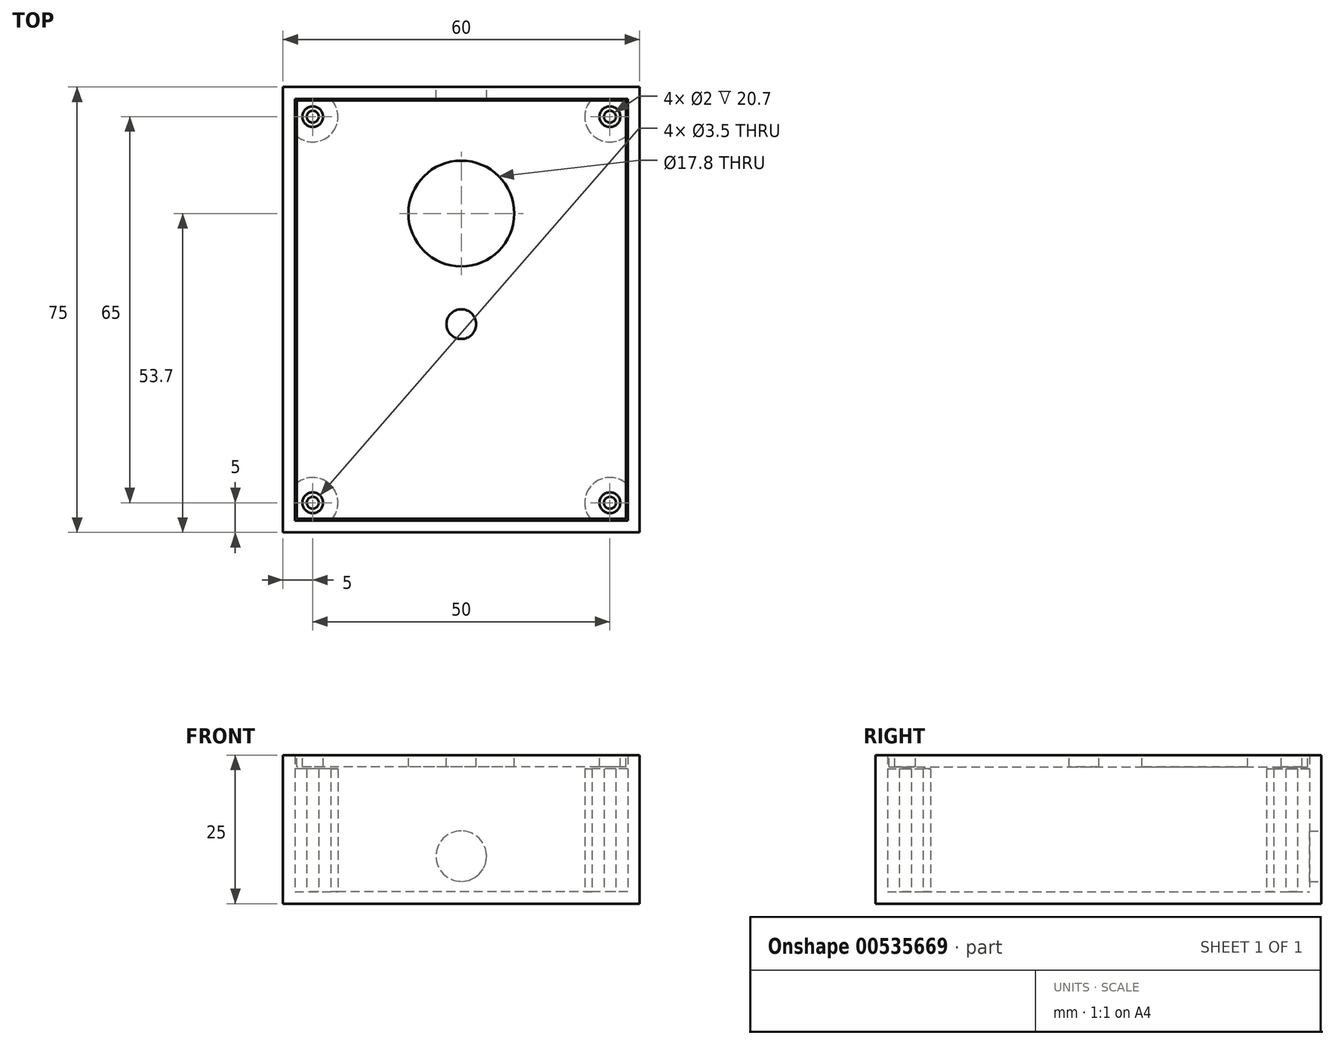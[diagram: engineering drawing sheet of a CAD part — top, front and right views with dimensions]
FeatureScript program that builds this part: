
annotation { "Feature Type Name" : "Feature", "Feature Type Description" : "" }
export const myFeature = defineFeature(function(context is Context, id is Id, definition is map)
    precondition{}
    {
        {
            var Q0;
            Q0=qCreatedBy(makeId("Top.planeOp"),FACE);
            var sketch = newSketch(context, id + "F0", { "sketchPlane" : qUnion([Q0])});
            skLineSegment(sketch, "E0.bottom", {"start": v(30, -37.5) * mm, "end": v(-30, -37.5) * mm});
            skLineSegment(sketch, "E0.top", {"start": v(30, 37.5) * mm, "end": v(-30, 37.5) * mm});
            skLineSegment(sketch, "E0.left", {"start": v(30, -37.5) * mm, "end": v(30, 37.5) * mm});
            skLineSegment(sketch, "E0.right", {"start": v(-30, -37.5) * mm, "end": v(-30, 37.5) * mm});
            skPoint(sketch, "E0.middle", {"position": v(0, 0) * mm});
            skSolve(sketch);
        }
        {
            var Q0;
            Q0 = qSketchRegion(id + "F0", true);
            extrude(context, id + "F1", {"entities" : qUnion([Q0]), "depth" : 25 * mm, "offsetDistance" : 25 * mm});
        }
        {
            var Q0;
            Q0=makeQuery(id+"F1.opExtrude","CAP_FACE",FACE,{"disambiguationData":[OSD([sQuery(id+"F0.wireOp",EDGE,"E0.bottom"),sQuery(id+"F0.wireOp",EDGE,"E0.top"),sQuery(id+"F0.wireOp",EDGE,"E0.left"),sQuery(id+"F0.wireOp",EDGE,"E0.right")])],"isStart":false});
            shell(context, id + "F2", {"entities" : qUnion([Q0]), "thickness" : 2 * mm});
        }
        {
            var Q0;
            Q0=makeQuery(id+"F2.opShell","OFFSET_FACE",FACE,{"disambiguationData":[OSD([sQuery(id+"F0.wireOp",EDGE,"E0.bottom"),sQuery(id+"F0.wireOp",EDGE,"E0.top"),sQuery(id+"F0.wireOp",EDGE,"E0.left"),sQuery(id+"F0.wireOp",EDGE,"E0.right")])]});
            var sketch = newSketch(context, id + "F3", { "sketchPlane" : qUnion([Q0])});
            skCircle(sketch, "E1", {"center": v(-25, -32.5) * mm, "radius": 1 * mm});
            skCircle(sketch, "E2", {"center": v(-25, -32.5) * mm, "radius": 4.25 * mm});
            skLineSegment(sketch, "E3", {"start": v(0, 35.5) * mm, "end": v(0, -35.5) * mm, "construction": true});
            skLineSegment(sketch, "E4", {"start": v(28, 0) * mm, "end": v(-28, 0) * mm, "construction": true});
            skCircle(sketch, "E5.MirrorC", {"center": v(25, -32.5) * mm, "radius": 4.25 * mm});
            skCircle(sketch, "E6.MirrorC", {"center": v(25, -32.5) * mm, "radius": 1 * mm});
            skCircle(sketch, "E7.MirrorC", {"center": v(25, 32.5) * mm, "radius": 4.25 * mm});
            skCircle(sketch, "E8.MirrorC", {"center": v(25, 32.5) * mm, "radius": 1 * mm});
            skCircle(sketch, "E9.MirrorC", {"center": v(-25, 32.5) * mm, "radius": 4.25 * mm});
            skCircle(sketch, "E10.MirrorC", {"center": v(-25, 32.5) * mm, "radius": 1 * mm});
            skSolve(sketch);
        }
        {
            var Q0;
            Q0 = qSketchRegion(id + "F3", true);
            extrude(context, id + "F4", {"entities" : qUnion([Q0]), "operationType" : NewBodyOperationType.ADD, "depth" : 20.7 * mm, "offsetDistance" : 25 * mm});
        }
        {
            var Q0;
            Q0=makeQuery(id+"F1.opExtrude","CAP_FACE",FACE,{"disambiguationData":[OSD([sQuery(id+"F0.wireOp",EDGE,"E0.bottom"),sQuery(id+"F0.wireOp",EDGE,"E0.top"),sQuery(id+"F0.wireOp",EDGE,"E0.left"),sQuery(id+"F0.wireOp",EDGE,"E0.right")])],"isStart":false});
            var sketch = newSketch(context, id + "F5", { "sketchPlane" : qUnion([Q0])});
            skLineSegment(sketch, "E11.0", {"start": v(27.7, 35.2) * mm, "end": v(-27.7, 35.2) * mm});
            skLineSegment(sketch, "E11.1", {"start": v(27.7, -35.2) * mm, "end": v(27.7, 35.2) * mm});
            skLineSegment(sketch, "E11.2", {"start": v(27.7, -35.2) * mm, "end": v(-27.7, -35.2) * mm});
            skLineSegment(sketch, "E11.3", {"start": v(-27.7, -35.2) * mm, "end": v(-27.7, 35.2) * mm});
            skCircle(sketch, "E12", {"center": v(-25, 32.5) * mm, "radius": 1.75 * mm});
            skCircle(sketch, "E13", {"center": v(25, 32.5) * mm, "radius": 1.75 * mm});
            skCircle(sketch, "E14", {"center": v(-25, -32.5) * mm, "radius": 1.75 * mm});
            skCircle(sketch, "E15", {"center": v(25, -32.5) * mm, "radius": 1.75 * mm});
            skSolve(sketch);
        }
        {
            var Q0;
            Q0 = qSketchRegion(id + "F5", true);
            extrude(context, id + "F6", {"entities" : qUnion([Q0]), "oppositeDirection" : true, "depth" : 2 * mm, "offsetDistance" : 25 * mm});
        }
        {
            var Q0;
            Q0=makeQuery(id+"F6.opExtrude","CAP_FACE",FACE,{"disambiguationData":[OSD([sQuery(id+"F5.wireOp",EDGE,"E11.0"),sQuery(id+"F5.wireOp",EDGE,"E11.1"),sQuery(id+"F5.wireOp",EDGE,"E11.2"),sQuery(id+"F5.wireOp",EDGE,"E11.3"),sQuery(id+"F5.wireOp",EDGE,"E12"),sQuery(id+"F5.wireOp",EDGE,"E13"),sQuery(id+"F5.wireOp",EDGE,"E14"),sQuery(id+"F5.wireOp",EDGE,"E15")])],"isStart":true});
            var sketch = newSketch(context, id + "F7", { "sketchPlane" : qUnion([Q0])});
            skCircle(sketch, "E16", {"center": v(0, 16.2) * mm, "radius": 8.9 * mm});
            skCircle(sketch, "E17", {"center": v(0, -2.43) * mm, "radius": 2.5 * mm});
            skSolve(sketch);
        }
        {
            var Q0;
            Q0 = qSketchRegion(id + "F7", true);
            extrude(context, id + "F8", {"entities" : qUnion([Q0]), "operationType" : NewBodyOperationType.REMOVE, "endBound" : BoundingType.UP_TO_NEXT, "oppositeDirection" : true, "depth" : 25 * mm, "offsetDistance" : 25 * mm});
        }
        {
            var Q0;
            Q0=makeQuery(id+"F1.opExtrude","SWEPT_FACE",FACE,{"disambiguationData":[OSD([sQuery(id+"F0.wireOp",EDGE,"E0.top")])]});
            var sketch = newSketch(context, id + "F9", { "sketchPlane" : qUnion([Q0])});
            skCircle(sketch, "E18", {"center": v(0, 8) * mm, "radius": 4.25 * mm});
            skPoint(sketch, "E18.centerSnap0", {"position": v(0, 0) * mm});
            skSolve(sketch);
        }
        {
            var Q0;
            Q0=makeQuery(id+"F9.imprint","IMPRINT",FACE,{"disambiguationData":[TD([[makeQuery(id+"F9.imprint","IMPRINT",EDGE,{"derivedFrom":sQuery(id+"F9.wireOp",EDGE,"E18")}),1.0]])]});
            extrude(context, id + "F10", {"entities" : qUnion([Q0]), "operationType" : NewBodyOperationType.REMOVE, "endBound" : BoundingType.UP_TO_NEXT, "oppositeDirection" : true, "depth" : 25 * mm, "offsetDistance" : 25 * mm});
        }
    });
